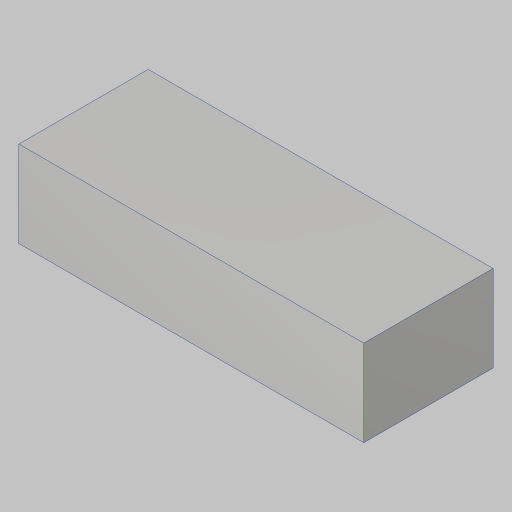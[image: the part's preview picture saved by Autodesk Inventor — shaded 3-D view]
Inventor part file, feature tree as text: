
AUTODESK INVENTOR PART (.ipt)
format: ipt  version: 2023.5 (Build 275446000, 446)  size: 87,552 bytes
history: native  units: in
note: dims shown in document units (in); Inventor stores cm internally (conversion verified against a paired STEP export)
features: extrude x1, sketch x1
ambient origin geometry x8: Origin, YZ Plane, XZ Plane, XY Plane, X Axis, Y Axis, Z Axis, Center Point
bodies: Solid1 (feature_tree)
feature tree (2):
  extrude  "Extrusion1"  Depth=3.0in
  sketch  "Sketch1"  dims[d0=8.0in d1=3.0in d2=2.0in d3=0.0in]
